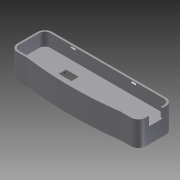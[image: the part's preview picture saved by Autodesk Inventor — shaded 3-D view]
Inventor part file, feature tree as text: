
AUTODESK INVENTOR PART (.ipt)
format: ipt  version: 2014 SP1 (Build 180222100, 222)  size: 397,824 bytes
history: native  units: mm
features: sketch x13, extrude x12, chamfer x4, other x2
ambient origin geometry x8: Origin, YZ Plane, XZ Plane, XY Plane, X Axis, Y Axis, Z Axis, Center Point
bodies: Solid1 (feature_tree)
feature tree (31):
  extrude  "Extrusion1"  Depth=38.0mm
  extrude  "Extrusion2"  Depth=19.0mm
  extrude  "Extrusion3"  Depth=8.0mm
  extrude  "Extrusion4"  Depth=8.0mm
  chamfer  "Chamfer1"  Distance=15.0mm
  chamfer  "Chamfer3"  Distance=14.0mm
  chamfer  "Chamfer4"  Distance=14.0mm
  chamfer  "Chamfer5"  Distance=1.0mm
  extrude  "Extrusion5"  Depth=2.0mm
  extrude  "Extrusion8"  TaperAngle=0.0deg  [1 undecoded]
  extrude  "Extrusion10"  TaperAngle=0.0deg  [1 undecoded]
  extrude  "Extrusion11"  Depth=2.0mm
  other  "Lip1"
  extrude  "Extrusion12"  TaperAngle=0.0deg  [1 undecoded]
  extrude  "Extrusion13"  Depth=5.0mm
  other  "Boss1"
  extrude  "Extrusion14"  Depth=5.0mm
  extrude  "Extrusion15"  Depth=2.0mm
  sketch  "Sketch1"  dims[d0=140.0mm d1=38.0mm]
  sketch  "Sketch2"  dims[d2=70.0mm d3=19.0mm]
  sketch  "Sketch3"  dims[d4=8.0mm d5=8.0mm]
  sketch  "Sketch4"  dims[d6=8.0mm d7=8.0mm d8=15.0mm d9=0.0mm]
  sketch  "Sketch5"  dims[d10=2.0mm d11=14.0mm d12=0.0mm]
  sketch  "Sketch8"  dims[d13=6.915756mm]
  sketch  "Sketch11"  dims[d14=10.0mm]
  sketch  "Sketch12"  dims[d15=15.0mm]
  sketch  "Sketch13"  dims[d16=7.5mm d17=14.0mm d18=0.0mm]
  sketch  "Sketch14"  dims[d19=38.0mm]
  sketch  "Sketch15"  dims[d20=5.0mm]
  sketch  "Sketch16"  dims[d21=5.0mm]
  sketch  "Sketch17"  dims[d22=38.0mm d23=1.0mm d24=1.0mm d25=0.0mm d26=0.0mm d28=1.0mm d29=0.0mm d30=5.0mm d31=5.0mm d33=1.0mm d34=0.0mm d36=13.0mm d37=0.0mm d38=1.0mm d39=1.0mm d40=45.0deg d44=1.0mm d45=1.0mm d46=45.0deg d47=1.0mm d48=1.0mm d49=45.0deg d50=1.0mm d51=1.0mm d52=45.0deg d53=10.0mm d54=5.0mm d55=11.0mm d56=0.0mm d59=66.0mm d60=74.0mm d63=2.0mm d64=18.0mm d65=18.0mm d66=5.5mm d67=30.0mm d68=30.0mm d69=10.0mm d70=0.0mm d78=35.0mm d79=14.0mm d80=12.0mm d81=13.0mm d82=10.0mm d83=0.0mm d84=3.0mm d85=10.0mm d86=0.0mm d87=2.0mm d88=1.5mm d89=0.0mm d90=0.0mm d91=0.0mm d92=0.0mm d93=2.0mm d95=9.9mm d96=0.0mm d97=0.0mm d98=2.0mm d99=0.0mm d101=2.0mm d102=0.0mm d103=7.74mm d104=2.0mm d106=4.0mm d107=2.0mm d108=8.0mm d109=0.0mm d110=27.0mm d111=5.0mm d114=27.0mm d115=5.0mm d116=5.0mm d117=19.0mm d118=0.0mm d119=11.0mm d120=5.0mm d121=3.0mm d122=9.5mm d123=0.349066mm d124=0.174533mm d125=20.0mm d127=2.0mm d128=2.0mm d129=10.0mm d130=0.0mm d131=1.745329mm d132=0.436332mm d133=0.0mm d134=0.0mm d135=0.0mm d136=360.0deg d137=102.0mm d138=4.0mm d139=2.0mm d140=2.0mm d141=0.0mm d142=2.0mm d143=14.0mm d144=10.0mm d145=0.0mm d146=2.0mm d147=0.0mm d148=0.0mm d149=10.0mm d150=2.0mm d151=0.0mm]
note: 3 required parameter values undecoded (feature->parameter linkage not recoverable at this tier; creation-order binding heuristic only, values carry confidence <= 0.55)
